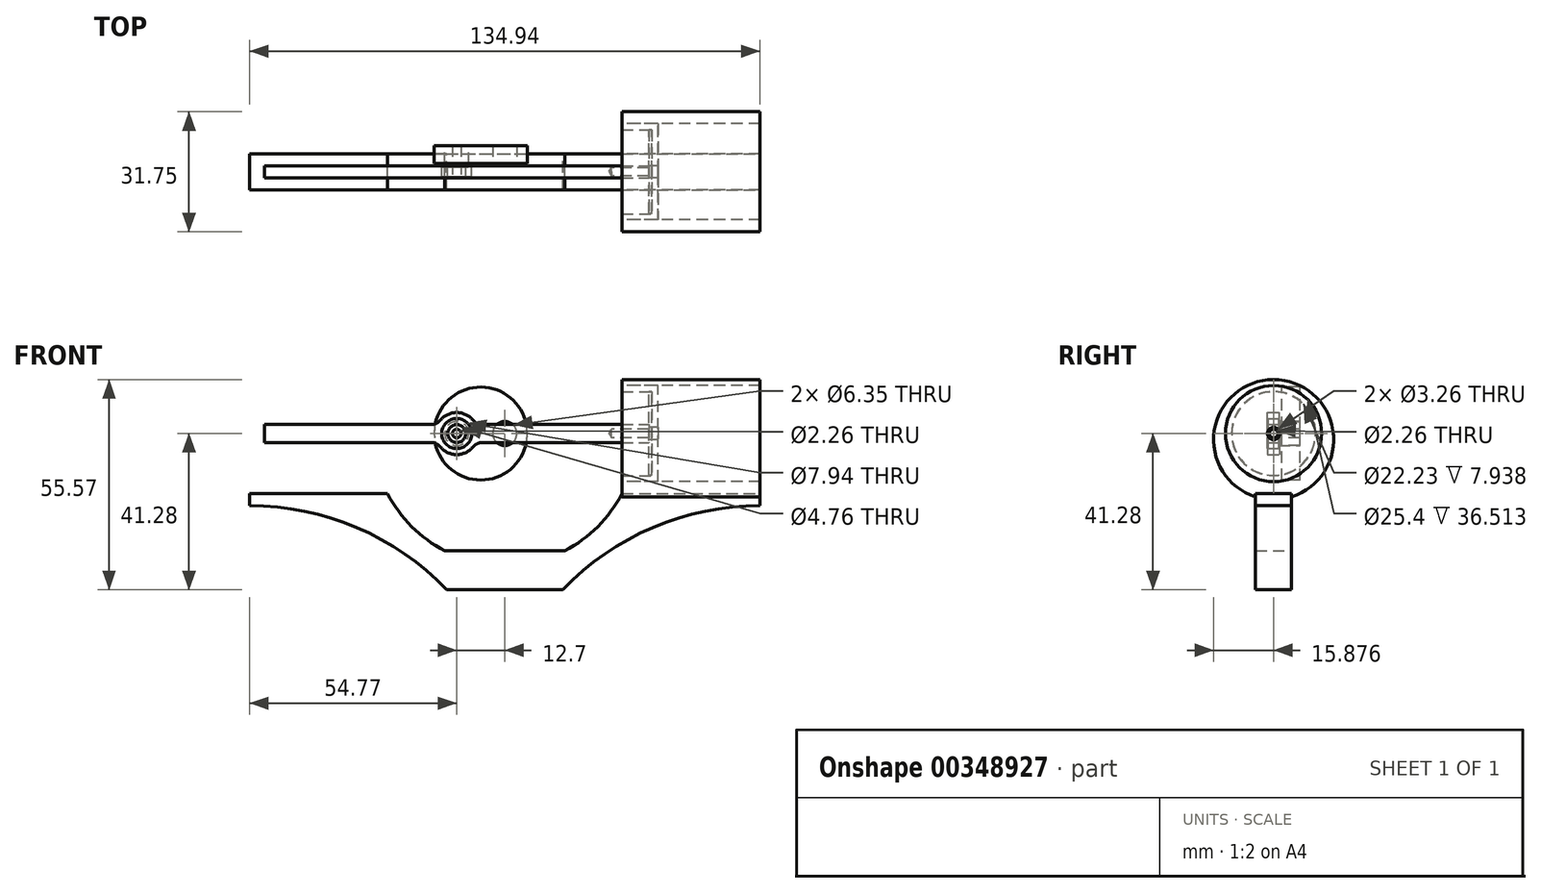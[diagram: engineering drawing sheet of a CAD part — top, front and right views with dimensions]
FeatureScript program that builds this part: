
annotation { "Feature Type Name" : "Feature", "Feature Type Description" : "" }
export const myFeature = defineFeature(function(context is Context, id is Id, definition is map)
    precondition{}
    {
        {
            var Q0;
            Q0=qCreatedBy(makeId("Front.planeOp"),FACE);
            var sketch = newSketch(context, id + "F0", { "sketchPlane" : qUnion([Q0])});
            skCircle(sketch, "E0", {"center": v(0, 0) * mm, "radius": 12.3 * mm});
            skPoint(sketch, "E1", {"position": v(-6.35, 0) * mm});
            skCircle(sketch, "E2", {"center": v(-6.35, 0) * mm, "radius": 3.18 * mm});
            skCircle(sketch, "E3.MirrorC", {"center": v(6.35, 0) * mm, "radius": 3.18 * mm});
            skSolve(sketch);
        }
        {
            var Q0;
            Q0=makeQuery(id+"F0.imprint","IMPRINT",FACE,{"disambiguationData":[TD([[makeQuery(id+"F0.imprint","IMPRINT",EDGE,{"derivedFrom":sQuery(id+"F0.wireOp",EDGE,"E0")}),1.0]])]});
            extrude(context, id + "F1", {"entities" : qUnion([Q0]), "oppositeDirection" : true, "depth" : 2.38 * mm, "hasSecondDirection" : true, "secondDirectionOppositeDirection" : false, "secondDirectionDepth" : 2.38 * mm});
        }
        {
            var Q0;
            Q0=makeQuery(id+"F1.opExtrude","CAP_FACE",FACE,{"disambiguationData":[OSD([sQuery(id+"F0.wireOp",EDGE,"E0"),sQuery(id+"F0.wireOp",EDGE,"E2"),sQuery(id+"F0.wireOp",EDGE,"E3.MirrorC")])],"isStart":false});
            var sketch = newSketch(context, id + "F2", { "sketchPlane" : qUnion([Q0])});
            skCircle(sketch, "E4.0", {"center": v(6.35, 0) * mm, "radius": 3.18 * mm});
            skSolve(sketch);
        }
        {
            var Q0;
            Q0=qSketchRegion(id+"F2",true);
            extrude(context, id + "F3", {"entities" : qUnion([Q0]), "oppositeDirection" : true, "depth" : 5.56 * mm});
        }
        {
            var Q0;
            Q0=makeQuery(id+"F3.opExtrude","CAP_FACE",FACE,{"disambiguationData":[OSD([sQuery(id+"F2.wireOp",EDGE,"E4.0")])],"isStart":false});
            var sketch = newSketch(context, id + "F4", { "sketchPlane" : qUnion([Q0])});
            skPoint(sketch, "E5.0", {"position": v(-6.35, 0) * mm});
            skCircle(sketch, "E6", {"center": v(-6.35, 0) * mm, "radius": 2.38 * mm});
            skSolve(sketch);
        }
        {
            var Q0;
            Q0=qSketchRegion(id+"F4",true);
            extrude(context, id + "F5", {"entities" : qUnion([Q0]), "operationType" : NewBodyOperationType.ADD, "depth" : 2.78 * mm});
        }
        {
            var Q0;
            Q0=makeQuery(id+"F3.opExtrude","CAP_FACE",FACE,{"disambiguationData":[OSD([sQuery(id+"F2.wireOp",EDGE,"E4.0")])],"isStart":true});
            var sketch = newSketch(context, id + "F6", { "sketchPlane" : qUnion([Q0])});
            skPoint(sketch, "E7.0", {"position": v(6.35, 0) * mm});
            skSolve(sketch);
        }
        {
            var Q0;
            Q0=sQuery(id+"F6.wireOp",VERTEX,"E7.0");
            var Q1;
            Q1=makeQuery(id+"F3.opExtrude","SWEPT_BODY",BODY,{"disambiguationData":[OSD([sQuery(id+"F2.wireOp",EDGE,"E4.0")])]});
            hole(context, id + "F7", {"style" : HoleStyle.SIMPLE, "endStyle" : HoleEndStyle.THROUGH, "standardTappedOrClearance" : lookupTablePath({ "standard" : "ANSI", "engagement" : "75%", "pitch" : "40 tpi", "size" : "#4", "type" : "Tapped" }), "standardBlindInLast" : lookupTablePath({ "standard" : "ANSI", "engagement" : "75%", "pitch" : "40 tpi", "size" : "#4", "type" : "Tapped" }), "holeDiameter" : 2.26 * mm, "showTappedDepth" : true, "tappedDepth" : 7.95 * mm, "tapClearance" : 3, "locations" : qUnion([Q0]), "scope" : qUnion([Q1]), "majorDiameter" : 2.84 * mm});
        }
        {
            var Q0;
            Q0=makeQuery(id+"F3.opExtrude","CAP_FACE",FACE,{"disambiguationData":[OSD([sQuery(id+"F2.wireOp",EDGE,"E4.0")])],"isStart":false});
            var sketch = newSketch(context, id + "F8", { "sketchPlane" : qUnion([Q0])});
            skCircle(sketch, "E8.0", {"center": v(-6.35, 0) * mm, "radius": 2.38 * mm});
            skCircle(sketch, "E9", {"center": v(-6.35, 0) * mm, "radius": 3.97 * mm});
            skSolve(sketch);
        }
        {
            var Q0;
            Q0=qSketchRegion(id+"F8",true);
            extrude(context, id + "F9", {"entities" : qUnion([Q0]), "depth" : 2.78 * mm});
        }
        {
            var Q0;
            Q0=makeQuery(id+"F9.opExtrude","CAP_FACE",FACE,{"disambiguationData":[OSD([sQuery(id+"F8.wireOp",EDGE,"E8.0"),sQuery(id+"F8.wireOp",EDGE,"E9")])],"isStart":false});
            cPlane(context, id + "F10", {"entities" : qUnion([Q0]), "cplaneType" : CPlaneType.OFFSET, "offset" : 1.39 * mm, "oppositeDirection" : true, "width" : 152.4 * mm, "height" : 152.4 * mm});
        }
        {
            var Q0;
            Q0=qCreatedBy(id+"F10.planeOp",FACE);
            var sketch = newSketch(context, id + "F11", { "sketchPlane" : qUnion([Q0])});
            skCircle(sketch, "E10.0", {"center": v(-6.35, 0) * mm, "radius": 3.97 * mm});
            skArc(sketch, "E11", {"start": v(-2.06, 3.54) * mm, "mid": v(-3.98, 5.03) * mm, "end": v(-6.35, 5.56) * mm});
            skLineSegment(sketch, "E12", {"start": v(-6.35, 0) * mm, "end": v(2.25, 0) * mm, "construction": true});
            skLineSegment(sketch, "E13.0", {"start": v(-6.35, 2.38) * mm, "end": v(-3.17, 2.38) * mm});
            skLineSegment(sketch, "E14", {"start": v(-6.35, 0) * mm, "end": v(-6.35, 8.1) * mm, "construction": true});
            skLineSegment(sketch, "E15.trimOffspring", {"start": v(0.39, 2.38) * mm, "end": v(44.45, 2.38) * mm});
            skPoint(sketch, "E16.0", {"position": v(6.35, 0) * mm});
            skCircle(sketch, "E17.0", {"center": v(0, 0) * mm, "radius": 12.3 * mm, "construction": true});
            skLineSegment(sketch, "E18", {"start": v(6.35, 0) * mm, "end": v(6.35, 7.85) * mm, "construction": true});
            skCircle(sketch, "E19.MirrorC", {"center": v(12.7, 0) * mm, "radius": 12.3 * mm, "construction": true});
            skLineSegment(sketch, "E20.MirrorCS", {"start": v(19.05, 0) * mm, "end": v(19.05, 8.1) * mm, "construction": true});
            skArc(sketch, "E21.MirrorCS", {"start": v(-2.06, -3.54) * mm, "mid": v(-3.98, -5.03) * mm, "end": v(-6.35, -5.56) * mm});
            skLineSegment(sketch, "E22.MirrorCS", {"start": v(0.39, -2.38) * mm, "end": v(44.45, -2.38) * mm});
            skLineSegment(sketch, "E23", {"start": v(44.45, 2.38) * mm, "end": v(44.45, -2.38) * mm});
            skArc(sketch, "E24.MirrorCS", {"start": v(-10.64, 3.54) * mm, "mid": v(-8.72, 5.03) * mm, "end": v(-6.35, 5.56) * mm});
            skArc(sketch, "E25.MirrorCS", {"start": v(-10.64, -3.54) * mm, "mid": v(-8.72, -5.03) * mm, "end": v(-6.35, -5.56) * mm});
            skLineSegment(sketch, "E26.MirrorCS", {"start": v(-13.09, -2.38) * mm, "end": v(-57.15, -2.38) * mm});
            skLineSegment(sketch, "E27.MirrorCS", {"start": v(-57.15, 2.38) * mm, "end": v(-57.15, -2.38) * mm});
            skLineSegment(sketch, "E28.MirrorCS", {"start": v(-13.09, 2.38) * mm, "end": v(-57.15, 2.38) * mm});
            skPoint(sketch, "E29.visualSharp", {"position": v(-1.33, 2.38) * mm});
            skArc(sketch, "E29.filletArc", {"start": v(-2.06, 3.54) * mm, "mid": v(-0.97, 2.68) * mm, "end": v(0.39, 2.38) * mm});
            skPoint(sketch, "E30.visualSharp", {"position": v(-1.33, -2.38) * mm});
            skArc(sketch, "E30.filletArc", {"start": v(0.39, -2.38) * mm, "mid": v(-0.97, -2.68) * mm, "end": v(-2.06, -3.54) * mm});
            skPoint(sketch, "E31.visualSharp", {"position": v(-11.37, -2.38) * mm});
            skArc(sketch, "E31.filletArc", {"start": v(-10.64, -3.54) * mm, "mid": v(-11.73, -2.68) * mm, "end": v(-13.09, -2.38) * mm});
            skPoint(sketch, "E32.visualSharp", {"position": v(-11.37, 2.38) * mm});
            skArc(sketch, "E32.filletArc", {"start": v(-13.09, 2.38) * mm, "mid": v(-11.73, 2.68) * mm, "end": v(-10.64, 3.54) * mm});
            skSolve(sketch);
        }
        {
            var Q0;
            Q0=qSketchRegion(id+"F11",true);
            extrude(context, id + "F12", {"entities" : qUnion([Q0]), "depth" : 1.59 * mm, "hasSecondDirection" : true, "secondDirectionOppositeDirection" : true, "secondDirectionDepth" : 1.59 * mm});
        }
        {
            var Q0;
            Q0=makeQuery(id+"F12.opExtrude","SWEPT_FACE",FACE,{"disambiguationData":[OSD([sQuery(id+"F11.wireOp",EDGE,"E23")])]});
            var sketch = newSketch(context, id + "F13", { "sketchPlane" : qUnion([Q0])});
            skPoint(sketch, "E33.0", {"position": v(-4.56, 2.38) * mm});
            skPoint(sketch, "E34.0", {"position": v(-4.56, -2.38) * mm});
            skLineSegment(sketch, "E35", {"start": v(-4.56, 2.38) * mm, "end": v(-4.56, -2.38) * mm, "construction": true});
            skPoint(sketch, "E36", {"position": v(-4.56, 0) * mm});
            skSolve(sketch);
        }
        {
            var Q0;
            Q0=sQuery(id+"F13.wireOp",VERTEX,"E36");
            var Q1;
            Q1=makeQuery(id+"F12.opExtrude","SWEPT_BODY",BODY,{"disambiguationData":[OSD([sQuery(id+"F11.wireOp",EDGE,"E10.0"),sQuery(id+"F11.wireOp",EDGE,"E11"),sQuery(id+"F11.wireOp",EDGE,"E15.trimOffspring"),sQuery(id+"F11.wireOp",EDGE,"E21.MirrorCS"),sQuery(id+"F11.wireOp",EDGE,"E22.MirrorCS"),sQuery(id+"F11.wireOp",EDGE,"E23"),sQuery(id+"F11.wireOp",EDGE,"E24.MirrorCS"),sQuery(id+"F11.wireOp",EDGE,"E25.MirrorCS"),sQuery(id+"F11.wireOp",EDGE,"E26.MirrorCS"),sQuery(id+"F11.wireOp",EDGE,"E27.MirrorCS"),sQuery(id+"F11.wireOp",EDGE,"E28.MirrorCS"),sQuery(id+"F11.wireOp",EDGE,"E29.filletArc"),sQuery(id+"F11.wireOp",EDGE,"E30.filletArc"),sQuery(id+"F11.wireOp",EDGE,"E31.filletArc"),sQuery(id+"F11.wireOp",EDGE,"E32.filletArc")])]});
            hole(context, id + "F14", {"style" : HoleStyle.SIMPLE, "endStyle" : HoleEndStyle.BLIND, "standardTappedOrClearance" : lookupTablePath({ "standard" : "ANSI", "engagement" : "75%", "pitch" : "40 tpi", "size" : "#4", "type" : "Tapped" }), "standardBlindInLast" : lookupTablePath({ "standard" : "ANSI", "engagement" : "75%", "pitch" : "40 tpi", "size" : "#4", "type" : "Tapped" }), "holeDiameter" : 2.26 * mm, "showTappedDepth" : true, "holeDepth" : 9.86 * mm, "tappedDepth" : 7.95 * mm, "tapClearance" : 3, "locations" : qUnion([Q0]), "scope" : qUnion([Q1]), "majorDiameter" : 2.84 * mm});
        }
        {
            var Q0;
            Q0=makeQuery(id+"F12.opExtrude","SWEPT_FACE",FACE,{"disambiguationData":[OSD([sQuery(id+"F11.wireOp",EDGE,"E23")])]});
            var sketch = newSketch(context, id + "F15", { "sketchPlane" : qUnion([Q0])});
            skPoint(sketch, "E37.0", {"position": v(-4.56, 0) * mm});
            skCircle(sketch, "E38", {"center": v(-4.56, 0) * mm, "radius": 11.05 * mm});
            skSolve(sketch);
        }
        {
            var Q0;
            Q0=qSketchRegion(id+"F15",true);
            extrude(context, id + "F16", {"entities" : qUnion([Q0]), "depth" : 0.8 * mm});
        }
        {
            var Q0;
            Q0=makeQuery(id+"F16.opExtrude","CAP_FACE",FACE,{"disambiguationData":[OSD([sQuery(id+"F15.wireOp",EDGE,"E38")])],"isStart":false});
            var sketch = newSketch(context, id + "F17", { "sketchPlane" : qUnion([Q0])});
            skPoint(sketch, "E39.0", {"position": v(-4.56, 0) * mm});
            skCircle(sketch, "E40", {"center": v(-4.56, 0) * mm, "radius": 12.7 * mm});
            skSolve(sketch);
        }
        {
            var Q0;
            Q0=qSketchRegion(id+"F17",true);
            extrude(context, id + "F18", {"entities" : qUnion([Q0]), "depth" : 1.59 * mm});
        }
        {
            var Q0;
            Q0=makeQuery(id+"F18.opExtrude","CAP_FACE",FACE,{"disambiguationData":[OSD([sQuery(id+"F17.wireOp",EDGE,"E40")])],"isStart":false});
            var sketch = newSketch(context, id + "F19", { "sketchPlane" : qUnion([Q0])});
            skCircle(sketch, "E41.0", {"center": v(-4.56, 0) * mm, "radius": 12.7 * mm, "construction": true});
            skSolve(sketch);
        }
        {
            var Q0;
            Q0=sQuery(id+"F19.wireOp",VERTEX,"E41.0.center");
            var Q1;
            Q1=makeQuery(id+"F18.opExtrude","SWEPT_BODY",BODY,{"disambiguationData":[OSD([sQuery(id+"F17.wireOp",EDGE,"E40")])]});
            var Q2;
            Q2=makeQuery(id+"F16.opExtrude","SWEPT_BODY",BODY,{"disambiguationData":[OSD([sQuery(id+"F15.wireOp",EDGE,"E38")])]});
            hole(context, id + "F20", {"style" : HoleStyle.SIMPLE, "endStyle" : HoleEndStyle.THROUGH, "standardTappedOrClearance" : lookupTablePath({ "standard" : "ANSI", "fit" : "Normal (ASME)", "size" : "#4", "type" : "Clearance" }), "standardBlindInLast" : lookupTablePath({ "fit" : "Free", "standard" : "ANSI", "size" : "#4", "type" : "Clearance" }), "holeDiameter" : 3.26 * mm, "tappedDepth" : 7.95 * mm, "tapClearance" : 3, "locations" : qUnion([Q0]), "scope" : qUnion([Q1, Q2])});
        }
        {
            var Q0;
            Q0=makeQuery(id+"F18.opExtrude","CAP_FACE",FACE,{"disambiguationData":[OSD([sQuery(id+"F17.wireOp",EDGE,"E40")])],"isStart":true});
            var sketch = newSketch(context, id + "F21", { "sketchPlane" : qUnion([Q0])});
            skCircle(sketch, "E42.0", {"center": v(4.56, 0) * mm, "radius": 12.7 * mm});
            skCircle(sketch, "E43", {"center": v(4.56, 0) * mm, "radius": 11.11 * mm});
            skSolve(sketch);
        }
        {
            var Q0;
            Q0=qSketchRegion(id+"F21",true);
            extrude(context, id + "F22", {"entities" : qUnion([Q0]), "operationType" : NewBodyOperationType.ADD, "depth" : 7.94 * mm});
        }
        {
            var Q0;
            Q0=makeQuery(id+"F22.opExtrude","CAP_FACE",FACE,{"disambiguationData":[OSD([sQuery(id+"F21.wireOp",EDGE,"E42.0"),sQuery(id+"F21.wireOp",EDGE,"E43")])],"isStart":false});
            var sketch = newSketch(context, id + "F23", { "sketchPlane" : qUnion([Q0])});
            skCircle(sketch, "E44.0", {"center": v(4.56, 0) * mm, "radius": 12.7 * mm});
            skLineSegment(sketch, "E45.0.0", {"start": v(6.15, -2.38) * mm, "end": v(6.15, -3.54) * mm, "construction": true});
            skLineSegment(sketch, "E45.0.1", {"start": v(6.15, -3.54) * mm, "end": v(6.15, -5.56) * mm, "construction": true});
            skLineSegment(sketch, "E45.0.2", {"start": v(6.15, -3.54) * mm, "end": v(6.15, -2.38) * mm, "construction": true});
            skLineSegment(sketch, "E45.0.4", {"start": v(6.15, -2.38) * mm, "end": v(6.15, 2.38) * mm, "construction": true});
            skLineSegment(sketch, "E45.0.6", {"start": v(6.15, 2.38) * mm, "end": v(6.15, 3.54) * mm, "construction": true});
            skLineSegment(sketch, "E45.0.7", {"start": v(6.15, 3.54) * mm, "end": v(6.15, 5.56) * mm, "construction": true});
            skLineSegment(sketch, "E45.0.8", {"start": v(6.15, 3.54) * mm, "end": v(6.15, 2.38) * mm, "construction": true});
            skLineSegment(sketch, "E45.0.10", {"start": v(6.15, 2.38) * mm, "end": v(6.15, -2.38) * mm, "construction": true});
            skLineSegment(sketch, "E46", {"start": v(4.56, 0) * mm, "end": v(22.6, 0) * mm, "construction": true});
            skLineSegment(sketch, "E47", {"start": v(4.56, 0) * mm, "end": v(4.56, 12.7) * mm, "construction": true});
            skLineSegment(sketch, "E48", {"start": v(4.56, 0) * mm, "end": v(4.56, -7.8) * mm, "construction": true});
            skPoint(sketch, "E49", {"position": v(4.56, -1.59) * mm});
            skArc(sketch, "E50", {"start": v(9.33, -16.73) * mm, "mid": v(4.56, 14.29) * mm, "end": v(-0.2, -16.73) * mm});
            skLineSegment(sketch, "E51.0", {"start": v(-0.2, -15.88) * mm, "end": v(9.33, -15.88) * mm});
            skLineSegment(sketch, "E52.0", {"start": v(9.33, -16.73) * mm, "end": v(9.33, -15.88) * mm});
            skLineSegment(sketch, "E53.MirrorCS", {"start": v(-0.2, -16.73) * mm, "end": v(-0.2, -15.88) * mm});
            skLineSegment(sketch, "E54.trimOffspring", {"start": v(-0.2, -11.77) * mm, "end": v(-0.2, 11.77) * mm});
            skLineSegment(sketch, "E55.trimOffspring", {"start": v(9.33, -11.77) * mm, "end": v(9.33, 11.77) * mm});
            skPoint(sketch, "E56.trimOffspring.end.orphan", {"position": v(10.91, 17.74) * mm});
            skPoint(sketch, "E57.trimOffspring.end.orphan", {"position": v(-1.79, 17.74) * mm});
            skSolve(sketch);
        }
        {
            var Q0;
            Q0=qSketchRegion(id+"F23",true);
            extrude(context, id + "F24", {"entities" : qUnion([Q0]), "oppositeDirection" : true, "depth" : 36.5 * mm});
        }
        {
            var Q0;
            Q0=qCreatedBy(makeId("Front.planeOp"),FACE);
            var sketch = newSketch(context, id + "F25", { "sketchPlane" : qUnion([Q0])});
            skLineSegment(sketch, "E58.0", {"start": v(37.3, -16.73) * mm, "end": v(37.3, 14.29) * mm, "construction": true});
            skCircle(sketch, "E59.0", {"center": v(6.35, 0) * mm, "radius": 3.18 * mm, "construction": true});
            skLineSegment(sketch, "E60.1.0", {"start": v(23.08, 30.96) * mm, "end": v(-7.94, 30.96) * mm, "construction": true});
            skLineSegment(sketch, "E60.2.0", {"start": v(-24.6, 16.73) * mm, "end": v(-24.6, -14.29) * mm, "construction": true});
            skLineSegment(sketch, "E60.3.0", {"start": v(-10.38, -30.96) * mm, "end": v(20.64, -30.96) * mm, "construction": true});
            skSolve(sketch);
        }
        {
            var Q0;
            Q0=qCreatedBy(id+"F10.planeOp",FACE);
            var sketch = newSketch(context, id + "F26", { "sketchPlane" : qUnion([Q0])});
            skLineSegment(sketch, "E61.0", {"start": v(6.35, -30.96) * mm, "end": v(22.22, -30.96) * mm});
            skPoint(sketch, "E62.0", {"position": v(6.35, 0) * mm});
            skLineSegment(sketch, "E63", {"start": v(6.35, -41.28) * mm, "end": v(21.7, -41.28) * mm});
            skLineSegment(sketch, "E64", {"start": v(6.35, 0) * mm, "end": v(6.35, -41.28) * mm, "construction": true});
            skLineSegment(sketch, "E65", {"start": v(6.35, -30.96) * mm, "end": v(6.35, -41.28) * mm});
            skLineSegment(sketch, "E66", {"start": v(37.3, -15.88) * mm, "end": v(73.82, -15.88) * mm});
            skLineSegment(sketch, "E67.0", {"start": v(37.3, -16.73) * mm, "end": v(37.3, 14.29) * mm, "construction": true});
            skLineSegment(sketch, "E68.0", {"start": v(73.82, -16.73) * mm, "end": v(73.82, 14.29) * mm, "construction": true});
            skArc(sketch, "E69", {"start": v(37.3, -15.87) * mm, "mid": v(30.95, -24.6) * mm, "end": v(22.22, -30.96) * mm});
            skLineSegment(sketch, "E70", {"start": v(73.82, -15.87) * mm, "end": v(73.82, -19.05) * mm});
            skArc(sketch, "E71", {"start": v(73.82, -19.05) * mm, "mid": v(45.48, -24.84) * mm, "end": v(21.7, -41.28) * mm});
            skLineSegment(sketch, "E72.MirrorCS", {"start": v(6.35, -41.28) * mm, "end": v(-9, -41.28) * mm});
            skLineSegment(sketch, "E73.MirrorCS", {"start": v(6.35, -30.96) * mm, "end": v(-9.52, -30.96) * mm});
            skArc(sketch, "E74.MirrorCS", {"start": v(-24.6, -15.87) * mm, "mid": v(-18.25, -24.6) * mm, "end": v(-9.52, -30.96) * mm});
            skLineSegment(sketch, "E75.MirrorCS", {"start": v(-24.6, -15.88) * mm, "end": v(-61.12, -15.88) * mm});
            skLineSegment(sketch, "E76.MirrorCS", {"start": v(-61.12, -15.88) * mm, "end": v(-61.12, -19.05) * mm});
            skArc(sketch, "E77.MirrorCS", {"start": v(-61.12, -19.05) * mm, "mid": v(-32.78, -24.84) * mm, "end": v(-9, -41.28) * mm});
            skCircle(sketch, "E78", {"center": v(6.35, 0) * mm, "radius": 41.28 * mm, "construction": true});
            skSolve(sketch);
        }
        {
            var Q0;
            Q0=qSketchRegion(id+"F26",true);
            extrude(context, id + "F27", {"entities" : qUnion([Q0]), "depth" : 4.76 * mm, "hasSecondDirection" : true, "secondDirectionOppositeDirection" : true, "secondDirectionDepth" : 4.76 * mm});
        }
        {
            var Q0;
            Q0=qCreatedBy(makeId("Front.planeOp"),FACE);
            cPlane(context, id + "F28", {"entities" : qUnion([Q0]), "cplaneType" : CPlaneType.OFFSET, "offset" : 4.56 * mm, "oppositeDirection" : true, "width" : 152.4 * mm, "height" : 152.4 * mm});
        }
    });
